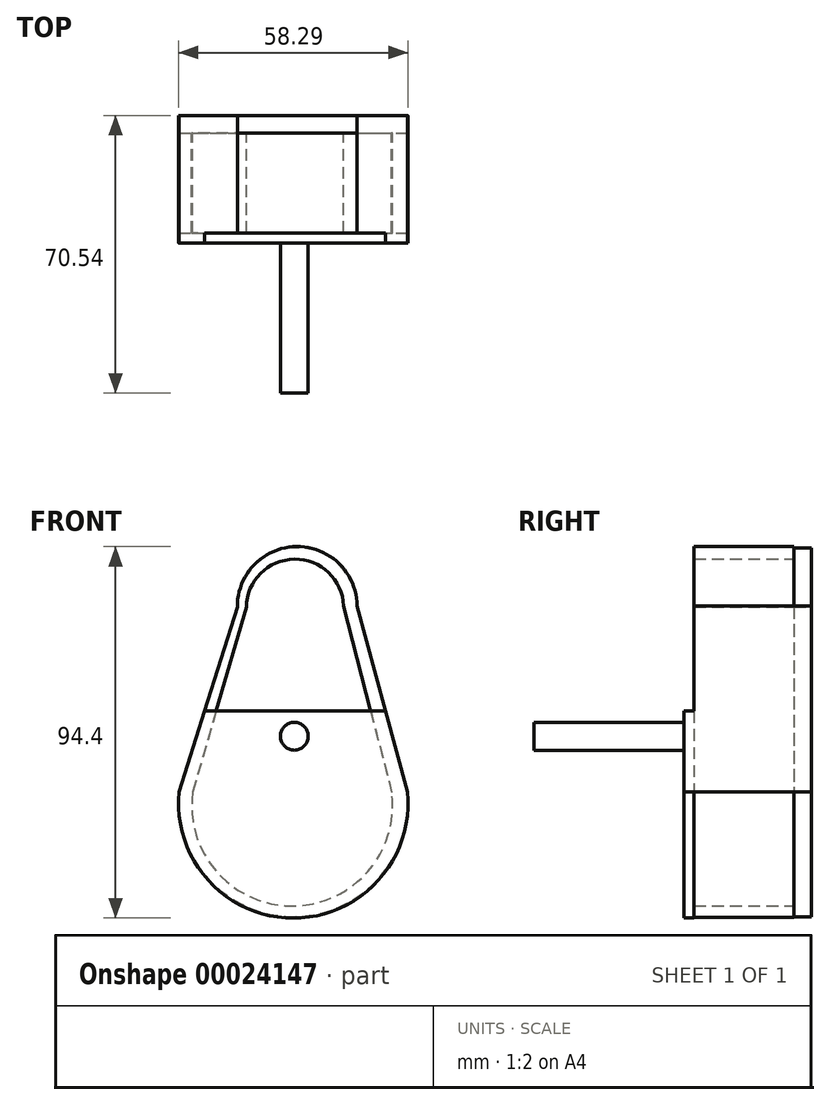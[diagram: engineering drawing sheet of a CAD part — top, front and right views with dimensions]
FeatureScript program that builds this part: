
annotation { "Feature Type Name" : "Feature", "Feature Type Description" : "" }
export const myFeature = defineFeature(function(context is Context, id is Id, definition is map)
    precondition{}
    {
        {
            var Q0;
            Q0=qCreatedBy(makeId("Front.planeOp"),FACE);
            var sketch = newSketch(context, id + "F0", { "sketchPlane" : qUnion([Q0])});
            skArc(sketch, "E0", {"start": v(10.35, 32.43) * mm, "mid": v(-5, 47.25) * mm, "end": v(-20.07, 32.15) * mm});
            skArc(sketch, "E1", {"start": v(-34.85, -14.75) * mm, "mid": v(-5.86, -46.49) * mm, "end": v(23.14, -14.75) * mm});
            skLineSegment(sketch, "E2", {"start": v(-20.07, 32.15) * mm, "end": v(-34.85, -14.75) * mm});
            skLineSegment(sketch, "E3", {"start": v(10.35, 32.43) * mm, "end": v(23.14, -14.75) * mm});
            skSolve(sketch);
        }
        {
            var Q0;
            Q0 = qSketchRegion(id + "F0", true);
            extrude(context, id + "F1", {"entities" : qUnion([Q0]), "depth" : 4.5 * mm});
        }
        {
            var Q0;
            Q0=makeQuery(id+"F1.opExtrude","CAP_FACE",FACE,{"disambiguationData":[OSD([sQuery(id+"F0.wireOp",EDGE,"E0"),sQuery(id+"F0.wireOp",EDGE,"E1"),sQuery(id+"F0.wireOp",EDGE,"E2"),sQuery(id+"F0.wireOp",EDGE,"E3")])],"isStart":false});
            var sketch = newSketch(context, id + "F2", { "sketchPlane" : qUnion([Q0])});
            skArc(sketch, "E4", {"start": v(10.35, 32.43) * mm, "mid": v(-5, 47.54) * mm, "end": v(-20.07, 32.15) * mm});
            skArc(sketch, "E5", {"start": v(-34.85, -14.75) * mm, "mid": v(-5.86, -46.63) * mm, "end": v(23.14, -14.75) * mm});
            skArc(sketch, "E6", {"start": v(6.94, 32.43) * mm, "mid": v(-5.57, 44.34) * mm, "end": v(-17.8, 32.15) * mm});
            skArc(sketch, "E7", {"start": v(-31.44, -14.91) * mm, "mid": v(-6.14, -43.77) * mm, "end": v(19.16, -14.91) * mm});
            skLineSegment(sketch, "E8", {"start": v(-20.07, 32.15) * mm, "end": v(-34.85, -14.75) * mm});
            skLineSegment(sketch, "E9", {"start": v(-17.8, 32.15) * mm, "end": v(-31.44, -14.91) * mm});
            skLineSegment(sketch, "E10", {"start": v(6.94, 32.43) * mm, "end": v(19.16, -14.91) * mm});
            skLineSegment(sketch, "E11", {"start": v(10.35, 32.43) * mm, "end": v(23.14, -14.75) * mm});
            skSolve(sketch);
        }
        {
            var Q0;
            Q0 = qSketchRegion(id + "F2", true);
            extrude(context, id + "F3", {"entities" : qUnion([Q0]), "operationType" : NewBodyOperationType.ADD, "depth" : 25.4 * mm});
        }
        {
            var Q0;
            Q0=makeQuery(id+"F3.opExtrude","CAP_FACE",FACE,{"disambiguationData":[OSD([sQuery(id+"F2.wireOp",EDGE,"E4"),sQuery(id+"F2.wireOp",EDGE,"E5"),sQuery(id+"F2.wireOp",EDGE,"E6"),sQuery(id+"F2.wireOp",EDGE,"E7"),sQuery(id+"F2.wireOp",EDGE,"E8"),sQuery(id+"F2.wireOp",EDGE,"E9"),sQuery(id+"F2.wireOp",EDGE,"E10"),sQuery(id+"F2.wireOp",EDGE,"E11")])],"isStart":false});
            var sketch = newSketch(context, id + "F4", { "sketchPlane" : qUnion([Q0])});
            skArc(sketch, "E12", {"start": v(-34.85, -14.75) * mm, "mid": v(-5.86, -46.85) * mm, "end": v(23.14, -14.75) * mm});
            skLineSegment(sketch, "E13", {"start": v(-34.85, -14.75) * mm, "end": v(-28.38, 5.76) * mm});
            skLineSegment(sketch, "E14", {"start": v(-28.38, 5.76) * mm, "end": v(17.58, 5.76) * mm});
            skLineSegment(sketch, "E15", {"start": v(17.58, 5.76) * mm, "end": v(23.14, -14.75) * mm});
            skSolve(sketch);
        }
        {
            var Q0;
            Q0 = qSketchRegion(id + "F4", true);
            extrude(context, id + "F5", {"entities" : qUnion([Q0]), "operationType" : NewBodyOperationType.ADD, "depth" : 2.54 * mm});
        }
        {
            var Q0;
            Q0=makeQuery(id+"F5.opExtrude","CAP_FACE",FACE,{"disambiguationData":[OSD([sQuery(id+"F4.wireOp",EDGE,"E12"),sQuery(id+"F4.wireOp",EDGE,"E13"),sQuery(id+"F4.wireOp",EDGE,"E14"),sQuery(id+"F4.wireOp",EDGE,"E15")])],"isStart":false});
            var sketch = newSketch(context, id + "F6", { "sketchPlane" : qUnion([Q0])});
            skCircle(sketch, "E16", {"center": v(-5.58, -0.66) * mm, "radius": 3.53 * mm});
            skSolve(sketch);
        }
        {
            var Q0;
            Q0 = qSketchRegion(id + "F6", true);
            extrude(context, id + "F7", {"entities" : qUnion([Q0]), "operationType" : NewBodyOperationType.ADD, "depth" : 38.1 * mm});
        }
    });
